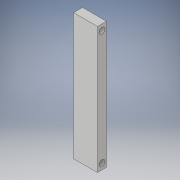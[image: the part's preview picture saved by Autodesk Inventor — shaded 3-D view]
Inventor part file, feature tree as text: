
AUTODESK INVENTOR PART (.ipt)
format: ipt  version: 2017 (Build 210142000, 142)  size: 98,816 bytes
history: native  units: in
note: dims shown in document units (in); Inventor stores cm internally (conversion verified against a paired STEP export)
features: extrude x1, sketch x1
ambient origin geometry x8: Origin, YZ Plane, XZ Plane, XY Plane, X Axis, Y Axis, Z Axis, Center Point
bodies: Solid1 (feature_tree)
feature tree (2):
  extrude  "Extrusion1"  Depth=0.75in
  sketch  "Sketch1"  dims[d0=10.6in d1=0.75in d2=0.5in d3=0.5in d4=0.5in d5=0.5in d6=2.0in d7=0.0in]
